# Revit family: Storage-Teknion-CCCH_Configurable_Cabinet-R2021
name_source: partatom
category: Furniture
units: mm (PartAtom-declared; Revit-internal decimal feet)

## family parameters
Always vertical = Yes
Cut with Voids When Loaded = No
OmniClass Number = 23.40.20.00
OmniClass Title = General Furniture and Specialties
Room Calculation Point = No
Shared = Yes
Work Plane-Based = No

## types (8) — shared parameters
Assembly Code = E2020200
Manufacturer = Teknion
Manufacturer Fax = 416.661.4586
Part Number = CCCH
Series = Chronicle
Sustainability Data = https://www.teknion.com
URL = www.teknion.com
Unit Weight URL = http://www.teknion.com
Warranty = http://www.teknion.com
zero-valued in all types: Default Elevation

## per-type parameters (varying)
- 2 Box, 1 File Drawer: (B) 2 Box, 1 File Drawer=Yes; (F) 2 File Drawers=No; (H) Double Hinged Doors=No; (L) Single Hinged Door - Left=No; (O) Open=No; (P) Hinged Doors with Printer Shelf=No; (R) Single Hinged Door - Right=No; 2D - Door 1=Yes; 2D - Door 2=No; 2D - Drawer=Yes; Case - Back (Open)=No; Case - Top=Yes; Cut-Out - Front - 1=5 "; Cut-Out - Front - 2=5 "; Cut-Out - Front - 3=0.5 "; Description=Configurable Cabinet, 2 Box, 1 File Drawer Storage Configuration; Dim - Case 1=0.843 "; Dim 1 - Case - Back=1.5 "; Dim 2 - Case - Back=1.539 "; Distance - Shelf Panel=1.843 "; Drawer 1=Yes; Drawer 2=No; Drawer 3=Yes; Drawer 4=Yes; Front=Yes; Model=CCCHB___; Shelf - Hinged Doors & Open=No
- 2 File Drawers: (B) 2 Box, 1 File Drawer=No; (F) 2 File Drawers=Yes; (H) Double Hinged Doors=No; (L) Single Hinged Door - Left=No; (O) Open=No; (P) Hinged Doors with Printer Shelf=No; (R) Single Hinged Door - Right=No; 2D - Door 1=Yes; 2D - Door 2=No; 2D - Drawer=Yes; Case - Back (Open)=No; Case - Top=Yes; Cut-Out - Front - 1=5 "; Cut-Out - Front - 2=0.5 "; Cut-Out - Front - 3=0.5 "; Description=Configurable Cabinet, 2 File Drawers Storage Configuration; Dim - Case 1=0.843 "; Dim 1 - Case - Back=1.5 "; Dim 2 - Case - Back=1.539 "; Distance - Shelf Panel=1.843 "; Drawer 1=Yes; Drawer 2=Yes; Drawer 3=No; Drawer 4=No; Front=Yes; Model=CCCHF___; Shelf - Hinged Doors & Open=No
- Double Hinged Doors: (B) 2 Box, 1 File Drawer=No; (F) 2 File Drawers=No; (H) Double Hinged Doors=Yes; (L) Single Hinged Door - Left=No; (O) Open=No; (P) Hinged Doors with Printer Shelf=No; (R) Single Hinged Door - Right=No; 2D - Door 1=No; 2D - Door 2=Yes; 2D - Drawer=No; Case - Back (Open)=No; Case - Top=Yes; Cut-Out - Front - 1=0.5 "; Cut-Out - Front - 2=0.5 "; Cut-Out - Front - 3=6 "; Description=Configurable Cabinet, Double Hinged Doors Storage Configuration; Dim - Case 1=0.843 "; Dim 1 - Case - Back=1.5 "; Dim 2 - Case - Back=1.539 "; Distance - Shelf Panel=1.843 "; Drawer 1=No; Drawer 2=No; Drawer 3=No; Drawer 4=No; Front=Yes; Model=CCCHH___; Shelf - Hinged Doors & Open=Yes
- Single Hinged Door - Left: (B) 2 Box, 1 File Drawer=No; (F) 2 File Drawers=No; (H) Double Hinged Doors=No; (L) Single Hinged Door - Left=Yes; (O) Open=No; (P) Hinged Doors with Printer Shelf=No; (R) Single Hinged Door - Right=No; 2D - Door 1=No; 2D - Door 2=No; 2D - Drawer=No; Case - Back (Open)=No; Case - Top=Yes; Cut-Out - Front - 1=0.5 "; Cut-Out - Front - 2=0.5 "; Cut-Out - Front - 3=0.5 "; Description=Configurable Cabinet, Single Hinged Door - Left Storage Configuration; Dim - Case 1=0.843 "; Dim 1 - Case - Back=1.5 "; Dim 2 - Case - Back=1.539 "; Distance - Shelf Panel=1.843 "; Drawer 1=No; Drawer 2=No; Drawer 3=No; Drawer 4=No; Front=Yes; Model=CCCHL___; Shelf - Hinged Doors & Open=Yes
- Single Hinged Door - Right: (B) 2 Box, 1 File Drawer=No; (F) 2 File Drawers=No; (H) Double Hinged Doors=No; (L) Single Hinged Door - Left=No; (O) Open=No; (P) Hinged Doors with Printer Shelf=No; (R) Single Hinged Door - Right=Yes; 2D - Door 1=No; 2D - Door 2=No; 2D - Drawer=No; Case - Back (Open)=No; Case - Top=Yes; Cut-Out - Front - 1=0.5 "; Cut-Out - Front - 2=0.5 "; Cut-Out - Front - 3=0.5 "; Description=Configurable Cabinet, Single Hinged Door - Right Storage Configuration; Dim - Case 1=0.843 "; Dim 1 - Case - Back=1.5 "; Dim 2 - Case - Back=1.539 "; Distance - Shelf Panel=1.843 "; Drawer 1=No; Drawer 2=No; Drawer 3=No; Drawer 4=No; Front=Yes; Model=CCCHR___; Shelf - Hinged Doors & Open=Yes
- Hinged Doors with Printer Shelf: (B) 2 Box, 1 File Drawer=No; (F) 2 File Drawers=No; (H) Double Hinged Doors=No; (L) Single Hinged Door - Left=No; (O) Open=No; (P) Hinged Doors with Printer Shelf=Yes; (R) Single Hinged Door - Right=No; 2D - Door 1=No; 2D - Door 2=Yes; 2D - Drawer=No; Case - Back (Open)=No; Case - Top=Yes; Cut-Out - Front - 1=0.5 "; Cut-Out - Front - 2=0.5 "; Cut-Out - Front - 3=6 "; Description=Configurable Cabinet, Hinged Doors with Printer Shelf Storage Configuration; Dim - Case 1=0.843 "; Dim 1 - Case - Back=1.5 "; Dim 2 - Case - Back=1.539 "; Distance - Shelf Panel=1.843 "; Drawer 1=No; Drawer 2=No; Drawer 3=No; Drawer 4=No; Front=Yes; Model=CCCHP___; Shelf - Hinged Doors & Open=No
- Open: (B) 2 Box, 1 File Drawer=No; (F) 2 File Drawers=No; (H) Double Hinged Doors=No; (L) Single Hinged Door - Left=No; (O) Open=Yes; (P) Hinged Doors with Printer Shelf=No; (R) Single Hinged Door - Right=No; 2D - Door 1=No; 2D - Door 2=No; 2D - Drawer=No; Case - Back (Open)=Yes; Case - Top=No; Cut-Out - Front - 1=0.5 "; Cut-Out - Front - 2=0.5 "; Cut-Out - Front - 3=0.5 "; Description=Configurable Cabinet, Open Storage Configuration; Dim - Case 1=0 "; Dim 1 - Case - Back=5.5 "; Dim 2 - Case - Back=1.854 "; Distance - Shelf Panel=1 "; Drawer 1=No; Drawer 2=No; Drawer 3=No; Drawer 4=No; Front=No; Model=CCCHO___; Shelf - Hinged Doors & Open=Yes
- Waste Bin Drawer: (B) 2 Box, 1 File Drawer=No; (F) 2 File Drawers=No; (H) Double Hinged Doors=No; (L) Single Hinged Door - Left=No; (O) Open=No; (P) Hinged Doors with Printer Shelf=No; (R) Single Hinged Door - Right=No; 2D - Door 1=Yes; 2D - Door 2=No; 2D - Drawer=Yes; Case - Back (Open)=No; Case - Top=Yes; Cut-Out - Front - 1=0.5 "; Cut-Out - Front - 2=5 "; Cut-Out - Front - 3=0.5 "; Description=Configurable Cabinet, Waste Bin Drawer Storage Configuration; Dim - Case 1=0.843 "; Dim 1 - Case - Back=1.5 "; Dim 2 - Case - Back=1.539 "; Distance - Shelf Panel=1.843 "; Drawer 1=No; Drawer 2=No; Drawer 3=No; Drawer 4=Yes; Front=Yes; Model=CCCHW___; Shelf - Hinged Doors & Open=No

type visibility flags (boolean, named after types; folded from table):
- 2 Box, 1 File Drawer: Yes: (none)
- 2 File Drawers: Yes: (none)
- Double Hinged Doors: Yes: (none)
- Single Hinged Door - Left: Yes: (none)
- Single Hinged Door - Right: Yes: (none)
- Hinged Doors with Printer Shelf: Yes: (none)
- Open: Yes: (none)
- Waste Bin Drawer: Yes: Waste Bin Drawer (W)

## geometry (parser evidence)
native form markers: Sweep x4
no freeform markers — native parametric forms only
